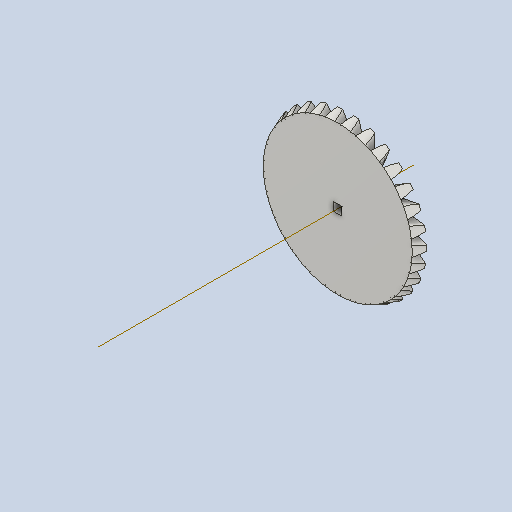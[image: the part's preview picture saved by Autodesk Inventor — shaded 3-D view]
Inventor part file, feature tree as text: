
AUTODESK INVENTOR PART (.ipt)
format: ipt  version: 2022 (Build 260153000, 153)  size: 679,424 bytes
history: native  units: in
note: dims shown in document units (in); Inventor stores cm internally (conversion verified against a paired STEP export)
features: other x30, sketch x3
ambient origin geometry x8: Origin, YZ Plane, XZ Plane, XY Plane, X Axis, Y Axis, Z Axis, Center Point
bodies: Solid1 (feature_tree)
feature tree (33):
  other  "Bevel Gear21_MIR1_MIR.ipt"
  other  "Solid1::Bevel Gear21_MIR1_MIR.ipt"
  other  "TaggingFeature1"
  other  "Teeth Body Sketch"
  other  "Start Sketch"
  other  "End Sketch"
  other  "End Sketch Right"
  other  "End Sketch Left"
  other  "Body Sketch"
  sketch  "Sketch6"  dims[d0=0.3937in]
  sketch  "Sketch8"  dims[d48=0.0in d49=0.0in d50=90.0deg d52=0.0in d53=0.0in d54=0.0in]
  sketch  "Sketch9"
  other  "3D Sketch Right"
  other  "3D Sketch Left"
  other  "Mesh Plane"
  other  "Top Plane"
  other  "Mesh Plane2"
  other  "Tooth Plane"
  other  "End Plane"
  other  "End Plane Right"
  other  "End Plane Left"
  other  "Z Axis_1"
  other  "Top Point"
  other  "Start Point"
  other  "End Point"
  other  "Srf1"
  other  "Srf1::Derived"
  other  "Start plane iMate"
  other  "Mesh iMate2"
  other  "Axis Angle iMate"
  other  "Axis iMate"
  other  "Mesh iMate"
  other  "Intersection iMate"
